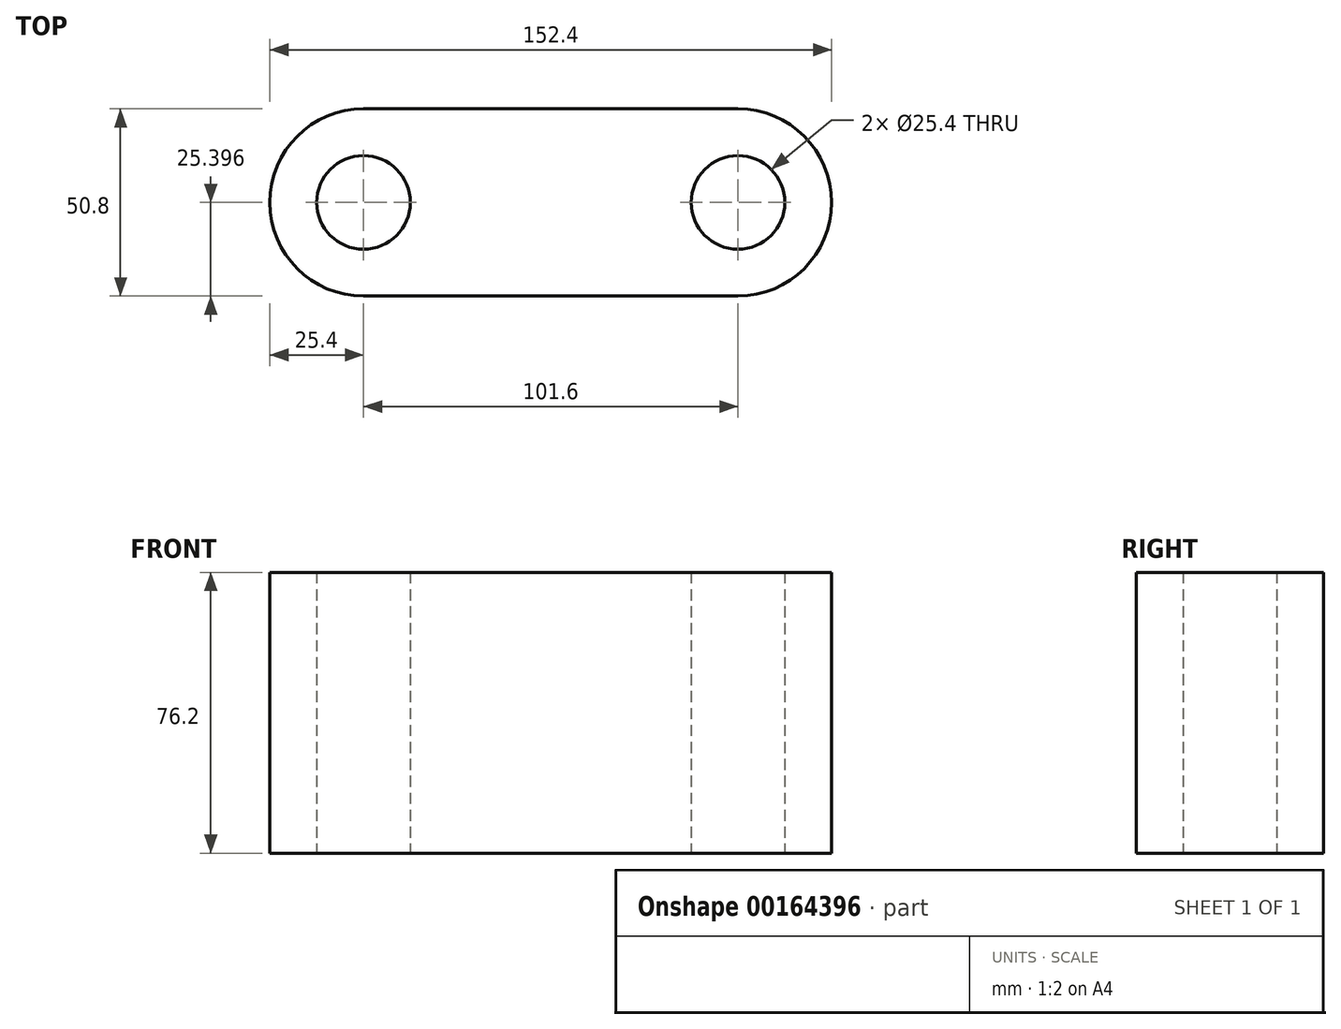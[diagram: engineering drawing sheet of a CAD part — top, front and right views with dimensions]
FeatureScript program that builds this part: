
annotation { "Feature Type Name" : "Feature", "Feature Type Description" : "" }
export const myFeature = defineFeature(function(context is Context, id is Id, definition is map)
    precondition{}
    {
        {
            var Q0;
            Q0=qCreatedBy(makeId("Top.planeOp"),FACE);
            var sketch = newSketch(context, id + "F0", { "sketchPlane" : qUnion([Q0])});
            skLineSegment(sketch, "E0", {"start": v(-41.9, 15.59) * mm, "end": v(59.7, 15.59) * mm});
            skLineSegment(sketch, "E1", {"start": v(-41.9, -35.21) * mm, "end": v(59.7, -35.21) * mm});
            skArc(sketch, "E2", {"start": v(-41.9, 15.59) * mm, "mid": v(-67.3, -9.81) * mm, "end": v(-41.9, -35.21) * mm});
            skArc(sketch, "E3", {"start": v(59.7, -35.21) * mm, "mid": v(85.1, -9.81) * mm, "end": v(59.7, 15.59) * mm});
            skCircle(sketch, "E4", {"center": v(-41.9, -9.81) * mm, "radius": 12.7 * mm});
            skCircle(sketch, "E5", {"center": v(59.7, -9.81) * mm, "radius": 12.7 * mm});
            skSolve(sketch);
        }
        {
            var Q0;
            Q0=makeQuery(id+"F0.imprint","IMPRINT",FACE,{"disambiguationData":[TD([[makeQuery(id+"F0.imprint","IMPRINT",EDGE,{"derivedFrom":sQuery(id+"F0.wireOp",EDGE,"E0")}),-1.0]])]});
            extrude(context, id + "F1", {"entities" : qUnion([Q0]), "depth" : 76.2 * mm});
        }
    });
